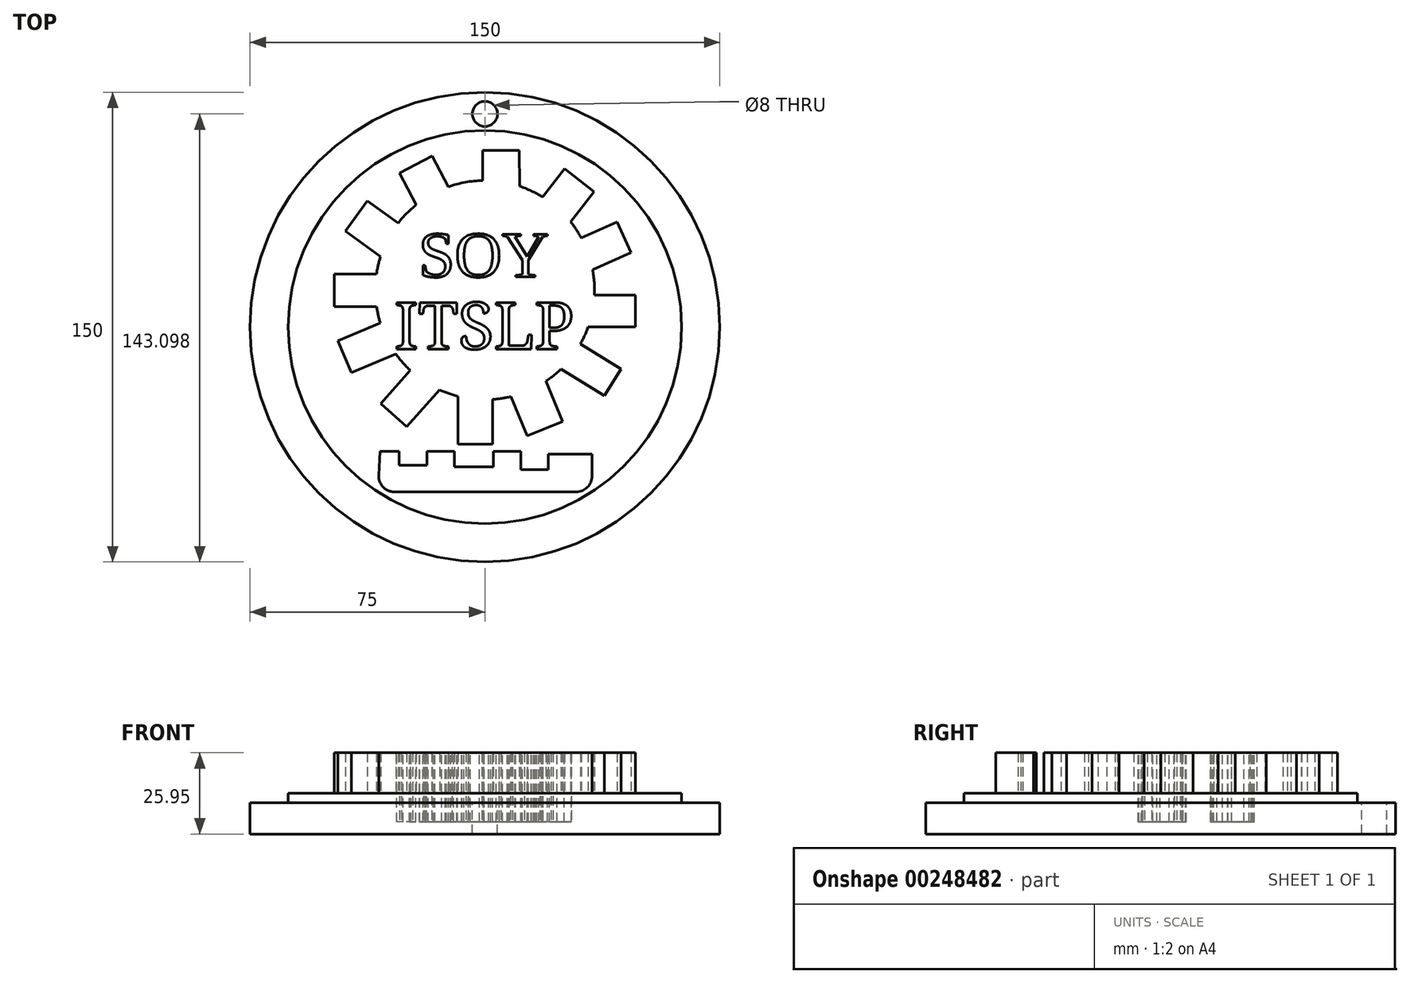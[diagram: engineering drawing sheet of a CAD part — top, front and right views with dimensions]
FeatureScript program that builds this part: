
annotation { "Feature Type Name" : "Feature", "Feature Type Description" : "" }
export const myFeature = defineFeature(function(context is Context, id is Id, definition is map)
    precondition{}
    {
        {
            var Q0;
            Q0=qCreatedBy(makeId("Top.planeOp"),FACE);
            var sketch = newSketch(context, id + "F0", { "sketchPlane" : qUnion([Q0])});
            skCircle(sketch, "E0", {"center": v(0, 0) * mm, "radius": 75 * mm});
            skSolve(sketch);
        }
        {
            var Q0;
            Q0=makeQuery(id+"F0.imprint","IMPRINT",FACE,{"disambiguationData":[TD([[makeQuery(id+"F0.imprint","IMPRINT",EDGE,{"derivedFrom":sQuery(id+"F0.wireOp",EDGE,"E0")}),1.0]])]});
            var sketch = newSketch(context, id + "F1", { "sketchPlane" : qUnion([Q0])});
            skCircle(sketch, "E1.0", {"center": v(0, 0) * mm, "radius": 62.8 * mm});
            skSolve(sketch);
        }
        {
            var Q0;
            Q0=makeQuery(id+"F0.imprint","IMPRINT",FACE,{"disambiguationData":[TD([[makeQuery(id+"F0.imprint","IMPRINT",EDGE,{"derivedFrom":sQuery(id+"F0.wireOp",EDGE,"E0")}),1.0]])]});
            extrude(context, id + "F2", {"entities" : qUnion([Q0]), "depth" : 10 * mm});
        }
        {
            var Q0;
            Q0 = qSketchRegion(id + "F1", true);
            extrude(context, id + "F3", {"entities" : qUnion([Q0]), "operationType" : NewBodyOperationType.ADD, "depth" : 13 * mm});
        }
        {
            var Q0;
            Q0=makeQuery(id+"F2.opExtrude","CAP_FACE",FACE,{"disambiguationData":[OSD([sQuery(id+"F0.wireOp",EDGE,"E0")])],"isStart":false});
            var sketch = newSketch(context, id + "F4", { "sketchPlane" : qUnion([Q0])});
            skLineSegment(sketch, "E2", {"start": v(-31.43, 68.1) * mm, "end": v(31.43, 68.1) * mm, "construction": true});
            skCircle(sketch, "E3", {"center": v(0, 68.1) * mm, "radius": 4 * mm});
            skSolve(sketch);
        }
        {
            var Q0;
            Q0=makeQuery(id+"F4.imprint","IMPRINT",FACE,{"disambiguationData":[TD([[makeQuery(id+"F4.imprint","IMPRINT",EDGE,{"derivedFrom":sQuery(id+"F4.wireOp",EDGE,"E3")}),1.0]])]});
            extrude(context, id + "F5", {"entities" : qUnion([Q0]), "operationType" : NewBodyOperationType.REMOVE, "oppositeDirection" : true, "depth" : 25.4 * mm});
        }
        {
            var Q0;
            Q0=makeQuery(id+"F3.opExtrude","CAP_FACE",FACE,{"disambiguationData":[OSD([sQuery(id+"F1.wireOp",EDGE,"E1.0")])],"isStart":false});
            var sketch = newSketch(context, id + "F6", { "sketchPlane" : qUnion([Q0])});
            skLineSegment(sketch, "E4", {"start": v(-61.69, 11.8) * mm, "end": v(61.69, 11.8) * mm, "construction": true});
            skArc(sketch, "E5", {"start": v(-0.68, 46.8) * mm, "mid": v(-6.24, 46.25) * mm, "end": v(-11.65, 44.81) * mm});
            skPoint(sketch, "E6.end.orphan", {"position": v(25.38, 50.6) * mm});
            skLineSegment(sketch, "E7", {"start": v(-0.68, 46.8) * mm, "end": v(-0.68, 56.4) * mm});
            skLineSegment(sketch, "E8", {"start": v(-0.68, 56.4) * mm, "end": v(10.94, 56.4) * mm});
            skLineSegment(sketch, "E9", {"start": v(10.94, 56.4) * mm, "end": v(11.06, 45.02) * mm});
            skLineSegment(sketch, "E10", {"start": v(18.4, 41.58) * mm, "end": v(25.38, 50.6) * mm});
            skLineSegment(sketch, "E11", {"start": v(25.38, 50.6) * mm, "end": v(34.85, 43.29) * mm});
            skLineSegment(sketch, "E12", {"start": v(34.85, 43.29) * mm, "end": v(27.38, 33.61) * mm});
            skLineSegment(sketch, "E13", {"start": v(30.77, 28.5) * mm, "end": v(42.2, 33.61) * mm});
            skLineSegment(sketch, "E14", {"start": v(42.2, 33.61) * mm, "end": v(46.6, 23.76) * mm});
            skLineSegment(sketch, "E15", {"start": v(46.6, 23.76) * mm, "end": v(34.4, 18.3) * mm});
            skArc(sketch, "E16.trimOffspring", {"start": v(18.4, 41.58) * mm, "mid": v(14.83, 43.51) * mm, "end": v(11.06, 45.02) * mm});
            skArc(sketch, "E17.trimOffspring", {"start": v(30.77, 28.5) * mm, "mid": v(29.18, 31.13) * mm, "end": v(27.38, 33.61) * mm});
            skLineSegment(sketch, "E18", {"start": v(34.97, 10.27) * mm, "end": v(48.04, 10.27) * mm});
            skLineSegment(sketch, "E19", {"start": v(48.04, 10.27) * mm, "end": v(48.04, 0) * mm});
            skLineSegment(sketch, "E20", {"start": v(48.04, 0) * mm, "end": v(32.95, 0) * mm});
            skLineSegment(sketch, "E21", {"start": v(30.5, -5.36) * mm, "end": v(43.43, -13.36) * mm});
            skLineSegment(sketch, "E22", {"start": v(43.43, -13.36) * mm, "end": v(38.14, -21.91) * mm});
            skLineSegment(sketch, "E23", {"start": v(38.14, -21.91) * mm, "end": v(24.32, -13.36) * mm});
            skLineSegment(sketch, "E24", {"start": v(19.5, -17.26) * mm, "end": v(24.8, -30.12) * mm});
            skLineSegment(sketch, "E25", {"start": v(24.8, -30.12) * mm, "end": v(13.44, -34.8) * mm});
            skLineSegment(sketch, "E26", {"start": v(13.44, -34.8) * mm, "end": v(8.24, -22.2) * mm});
            skLineSegment(sketch, "E27", {"start": v(2.4, -23.1) * mm, "end": v(2.4, -37.38) * mm});
            skLineSegment(sketch, "E28", {"start": v(2.4, -37.38) * mm, "end": v(-8.63, -37.38) * mm});
            skLineSegment(sketch, "E29", {"start": v(-8.63, -37.38) * mm, "end": v(-8.63, -22.1) * mm});
            skLineSegment(sketch, "E30", {"start": v(-14.45, -20.07) * mm, "end": v(-25, -31.83) * mm});
            skLineSegment(sketch, "E31", {"start": v(-25, -31.83) * mm, "end": v(-33.27, -24.4) * mm});
            skLineSegment(sketch, "E32", {"start": v(-33.27, -24.4) * mm, "end": v(-23.8, -13.85) * mm});
            skLineSegment(sketch, "E33", {"start": v(-28.44, -8.59) * mm, "end": v(-42.6, -14.56) * mm});
            skLineSegment(sketch, "E34", {"start": v(-42.6, -14.56) * mm, "end": v(-46.9, -4.36) * mm});
            skLineSegment(sketch, "E35", {"start": v(-46.9, -4.36) * mm, "end": v(-33.4, 1.34) * mm});
            skLineSegment(sketch, "E36", {"start": v(-34.6, 6.55) * mm, "end": v(-48.07, 6.55) * mm});
            skLineSegment(sketch, "E37", {"start": v(-48.07, 6.55) * mm, "end": v(-48.07, 16.96) * mm});
            skLineSegment(sketch, "E38", {"start": v(-48.07, 16.96) * mm, "end": v(-34.62, 16.96) * mm});
            skLineSegment(sketch, "E39", {"start": v(-33.32, 22.53) * mm, "end": v(-44.55, 30.62) * mm});
            skLineSegment(sketch, "E40", {"start": v(-44.55, 30.62) * mm, "end": v(-37.56, 40.33) * mm});
            skLineSegment(sketch, "E41", {"start": v(-37.56, 40.33) * mm, "end": v(-27.69, 33.22) * mm});
            skLineSegment(sketch, "E42", {"start": v(-21.96, 39.06) * mm, "end": v(-27.27, 49.15) * mm});
            skLineSegment(sketch, "E43", {"start": v(-27.27, 49.15) * mm, "end": v(-16.81, 54.65) * mm});
            skLineSegment(sketch, "E44", {"start": v(-16.81, 54.65) * mm, "end": v(-11.65, 44.81) * mm});
            skArc(sketch, "E45.trimOffspring", {"start": v(-21.96, 39.06) * mm, "mid": v(-25, 36.3) * mm, "end": v(-27.69, 33.22) * mm});
            skArc(sketch, "E46.trimOffspring", {"start": v(-33.32, 22.53) * mm, "mid": v(-34.08, 19.77) * mm, "end": v(-34.62, 16.96) * mm});
            skArc(sketch, "E47.trimOffspring", {"start": v(-34.6, 6.55) * mm, "mid": v(-34.1, 3.92) * mm, "end": v(-33.4, 1.34) * mm});
            skArc(sketch, "E48.trimOffspring", {"start": v(-28.44, -8.59) * mm, "mid": v(-26.26, -11.33) * mm, "end": v(-23.8, -13.85) * mm});
            skArc(sketch, "E49.trimOffspring", {"start": v(-14.45, -20.07) * mm, "mid": v(-11.59, -21.22) * mm, "end": v(-8.63, -22.1) * mm});
            skArc(sketch, "E50.trimOffspring", {"start": v(2.4, -23.1) * mm, "mid": v(5.34, -22.78) * mm, "end": v(8.24, -22.2) * mm});
            skArc(sketch, "E51.trimOffspring", {"start": v(19.5, -17.26) * mm, "mid": v(22, -15.41) * mm, "end": v(24.32, -13.36) * mm});
            skArc(sketch, "E52.trimOffspring", {"start": v(30.5, -5.36) * mm, "mid": v(31.84, -2.73) * mm, "end": v(32.95, 0) * mm});
            skArc(sketch, "E53.trimOffspring", {"start": v(34.97, 10.27) * mm, "mid": v(34.91, 14.3) * mm, "end": v(34.4, 18.3) * mm});
            skLineSegment(sketch, "E54", {"start": v(-28.83, -52.68) * mm, "end": v(29.12, -52.68) * mm});
            skLineSegment(sketch, "E55", {"start": v(34.2, -47.6) * mm, "end": v(34.2, -40.6) * mm});
            skLineSegment(sketch, "E56", {"start": v(34.2, -40.6) * mm, "end": v(20.29, -40.6) * mm});
            skLineSegment(sketch, "E57", {"start": v(20.29, -40.6) * mm, "end": v(20.29, -45.56) * mm});
            skLineSegment(sketch, "E58", {"start": v(20.29, -45.56) * mm, "end": v(11.52, -45.56) * mm});
            skLineSegment(sketch, "E59", {"start": v(11.52, -45.56) * mm, "end": v(11.52, -39.71) * mm});
            skLineSegment(sketch, "E60", {"start": v(11.52, -39.71) * mm, "end": v(2.76, -39.71) * mm});
            skLineSegment(sketch, "E61", {"start": v(2.76, -39.71) * mm, "end": v(2.76, -44.68) * mm});
            skLineSegment(sketch, "E62", {"start": v(2.76, -44.68) * mm, "end": v(-9.8, -44.68) * mm});
            skLineSegment(sketch, "E63", {"start": v(-9.8, -44.68) * mm, "end": v(-9.8, -39.71) * mm});
            skLineSegment(sketch, "E64", {"start": v(-9.8, -39.71) * mm, "end": v(-18.57, -39.71) * mm});
            skLineSegment(sketch, "E65", {"start": v(-18.57, -39.71) * mm, "end": v(-18.57, -44.1) * mm});
            skLineSegment(sketch, "E66", {"start": v(-18.57, -44.1) * mm, "end": v(-27.33, -44.1) * mm});
            skLineSegment(sketch, "E67", {"start": v(-27.33, -44.1) * mm, "end": v(-27.33, -39.71) * mm});
            skLineSegment(sketch, "E68", {"start": v(-27.33, -39.71) * mm, "end": v(-33.47, -39.71) * mm});
            skLineSegment(sketch, "E69", {"start": v(-33.47, -39.71) * mm, "end": v(-33.9, -47.31) * mm});
            skPoint(sketch, "E70.visualSharp", {"position": v(-34.2, -52.68) * mm});
            skArc(sketch, "E70.filletArc", {"start": v(-33.9, -47.31) * mm, "mid": v(-32.52, -51.09) * mm, "end": v(-28.83, -52.68) * mm});
            skPoint(sketch, "E71.visualSharp", {"position": v(34.2, -52.68) * mm});
            skArc(sketch, "E71.filletArc", {"start": v(29.12, -52.68) * mm, "mid": v(32.71, -51.2) * mm, "end": v(34.2, -47.6) * mm});
            skSolve(sketch);
        }
        {
            var Q0;
            Q0 = qSketchRegion(id + "F6", true);
            extrude(context, id + "F7", {"entities" : qUnion([Q0]), "operationType" : NewBodyOperationType.ADD, "depth" : 12.95 * mm});
        }
        {
            var Q0;
            Q0=makeQuery(id+"F7.opExtrude","CAP_FACE",FACE,{"disambiguationData":[OSD([sQuery(id+"F6.wireOp",EDGE,"E5"),sQuery(id+"F6.wireOp",EDGE,"E7"),sQuery(id+"F6.wireOp",EDGE,"E8"),sQuery(id+"F6.wireOp",EDGE,"E9"),sQuery(id+"F6.wireOp",EDGE,"E10"),sQuery(id+"F6.wireOp",EDGE,"E11"),sQuery(id+"F6.wireOp",EDGE,"E12"),sQuery(id+"F6.wireOp",EDGE,"E13"),sQuery(id+"F6.wireOp",EDGE,"E14"),sQuery(id+"F6.wireOp",EDGE,"E15"),sQuery(id+"F6.wireOp",EDGE,"E16.trimOffspring"),sQuery(id+"F6.wireOp",EDGE,"E17.trimOffspring"),sQuery(id+"F6.wireOp",EDGE,"E18"),sQuery(id+"F6.wireOp",EDGE,"E19"),sQuery(id+"F6.wireOp",EDGE,"E20"),sQuery(id+"F6.wireOp",EDGE,"E21"),sQuery(id+"F6.wireOp",EDGE,"E22"),sQuery(id+"F6.wireOp",EDGE,"E23"),sQuery(id+"F6.wireOp",EDGE,"E24"),sQuery(id+"F6.wireOp",EDGE,"E25"),sQuery(id+"F6.wireOp",EDGE,"E26"),sQuery(id+"F6.wireOp",EDGE,"E27"),sQuery(id+"F6.wireOp",EDGE,"E28"),sQuery(id+"F6.wireOp",EDGE,"E29"),sQuery(id+"F6.wireOp",EDGE,"E30"),sQuery(id+"F6.wireOp",EDGE,"E31"),sQuery(id+"F6.wireOp",EDGE,"E32"),sQuery(id+"F6.wireOp",EDGE,"E33"),sQuery(id+"F6.wireOp",EDGE,"E34"),sQuery(id+"F6.wireOp",EDGE,"E35"),sQuery(id+"F6.wireOp",EDGE,"E36"),sQuery(id+"F6.wireOp",EDGE,"E37"),sQuery(id+"F6.wireOp",EDGE,"E38"),sQuery(id+"F6.wireOp",EDGE,"E39"),sQuery(id+"F6.wireOp",EDGE,"E40"),sQuery(id+"F6.wireOp",EDGE,"E41"),sQuery(id+"F6.wireOp",EDGE,"E42"),sQuery(id+"F6.wireOp",EDGE,"E43"),sQuery(id+"F6.wireOp",EDGE,"E44"),sQuery(id+"F6.wireOp",EDGE,"E45.trimOffspring"),sQuery(id+"F6.wireOp",EDGE,"E46.trimOffspring"),sQuery(id+"F6.wireOp",EDGE,"E47.trimOffspring"),sQuery(id+"F6.wireOp",EDGE,"E48.trimOffspring"),sQuery(id+"F6.wireOp",EDGE,"E49.trimOffspring"),sQuery(id+"F6.wireOp",EDGE,"E50.trimOffspring"),sQuery(id+"F6.wireOp",EDGE,"E51.trimOffspring"),sQuery(id+"F6.wireOp",EDGE,"E52.trimOffspring"),sQuery(id+"F6.wireOp",EDGE,"E53.trimOffspring")])],"isStart":false});
            var sketch = newSketch(context, id + "F8", { "sketchPlane" : qUnion([Q0])});
            skText(sketch, "E72", { "text": "SOY", "fontName": "Tinos-Regular.ttf"});
            skLineSegment(sketch, "E73", {"start": v(-27.69, 33.22) * mm, "end": v(27.38, 33.61) * mm, "construction": true});
            const initialGuessF8  = {"E72": [-0.02122, 0.01605, 1, 0, 0.015]};
            skSetInitialGuess(sketch, initialGuessF8);
            skSolve(sketch);
        }
        {
            var Q0;
            Q0 = qSketchRegion(id + "F8", true);
            extrude(context, id + "F9", {"entities" : qUnion([Q0]), "operationType" : NewBodyOperationType.REMOVE, "oppositeDirection" : true, "depth" : 22.1 * mm});
        }
        {
            var Q0;
            {var subQ0=sQuery(id+"F6.wireOp",EDGE,"E24");var subQ1=sQuery(id+"F6.wireOp",EDGE,"E45.trimOffspring");var subQ2=sQuery(id+"F6.wireOp",EDGE,"E43");var subQ3=sQuery(id+"F6.wireOp",EDGE,"E27");var subQ4=sQuery(id+"F6.wireOp",EDGE,"E25");var subQ5=sQuery(id+"F6.wireOp",EDGE,"E46.trimOffspring");var subQ6=sQuery(id+"F6.wireOp",EDGE,"E19");var subQ7=sQuery(id+"F6.wireOp",EDGE,"E32");var subQ8=sQuery(id+"F6.wireOp",EDGE,"E9");var subQ9=sQuery(id+"F6.wireOp",EDGE,"E13");var subQ10=sQuery(id+"F6.wireOp",EDGE,"E18");var subQ11=sQuery(id+"F6.wireOp",EDGE,"E31");var subQ12=sQuery(id+"F6.wireOp",EDGE,"E12");var subQ13=sQuery(id+"F6.wireOp",EDGE,"E22");var subQ14=sQuery(id+"F6.wireOp",EDGE,"E7");var subQ15=sQuery(id+"F6.wireOp",EDGE,"E20");var subQ16=sQuery(id+"F6.wireOp",EDGE,"E14");var subQ17=sQuery(id+"F6.wireOp",EDGE,"E26");var subQ18=sQuery(id+"F6.wireOp",EDGE,"E47.trimOffspring");var subQ19=sQuery(id+"F6.wireOp",EDGE,"E33");var subQ20=sQuery(id+"F6.wireOp",EDGE,"E5");var subQ21=sQuery(id+"F6.wireOp",EDGE,"E23");var subQ22=sQuery(id+"F6.wireOp",EDGE,"E44");var subQ23=sQuery(id+"F6.wireOp",EDGE,"E10");var subQ24=sQuery(id+"F6.wireOp",EDGE,"E34");var subQ25=sQuery(id+"F6.wireOp",EDGE,"E8");var subQ26=sQuery(id+"F6.wireOp",EDGE,"E21");var subQ27=sQuery(id+"F6.wireOp",EDGE,"E28");var subQ28=sQuery(id+"F6.wireOp",EDGE,"E15");var subQ29=sQuery(id+"F6.wireOp",EDGE,"E41");var subQ30=sQuery(id+"F6.wireOp",EDGE,"E11");var subQ31=sQuery(id+"F6.wireOp",EDGE,"E16.trimOffspring");var subQ32=sQuery(id+"F6.wireOp",EDGE,"E29");var subQ33=sQuery(id+"F6.wireOp",EDGE,"E17.trimOffspring");var subQ34=sQuery(id+"F6.wireOp",EDGE,"E30");var subQ35=sQuery(id+"F6.wireOp",EDGE,"E35");var subQ36=sQuery(id+"F6.wireOp",EDGE,"E36");var subQ37=sQuery(id+"F6.wireOp",EDGE,"E37");var subQ38=sQuery(id+"F6.wireOp",EDGE,"E38");var subQ39=sQuery(id+"F6.wireOp",EDGE,"E42");var subQ40=sQuery(id+"F6.wireOp",EDGE,"E52.trimOffspring");var subQ41=sQuery(id+"F6.wireOp",EDGE,"E39");var subQ42=sQuery(id+"F6.wireOp",EDGE,"E53.trimOffspring");var subQ43=sQuery(id+"F6.wireOp",EDGE,"E40");var subQ44=sQuery(id+"F6.wireOp",EDGE,"E50.trimOffspring");var subQ45=sQuery(id+"F6.wireOp",EDGE,"E51.trimOffspring");var subQ46=sQuery(id+"F6.wireOp",EDGE,"E48.trimOffspring");var subQ47=sQuery(id+"F6.wireOp",EDGE,"E49.trimOffspring");Q0=makeQuery(id+"F9.boolean.opBoolean","SPLIT",FACE,{"disambiguationData":[TD([makeQuery(id+"F7.opExtrude","SWEPT_FACE",FACE,{"disambiguationData":[OSD([subQ20])]})])],"derivedFrom":makeQuery(id+"F7.opExtrude","CAP_FACE",FACE,{"disambiguationData":[OSD([subQ20,subQ14,subQ25,subQ8,subQ23,subQ30,subQ12,subQ9,subQ16,subQ28,subQ31,subQ33,subQ10,subQ6,subQ15,subQ26,subQ13,subQ21,subQ0,subQ4,subQ17,subQ3,subQ27,subQ32,subQ34,subQ11,subQ7,subQ19,subQ24,subQ35,subQ36,subQ37,subQ38,subQ41,subQ43,subQ29,subQ39,subQ2,subQ22,subQ1,subQ5,subQ18,subQ46,subQ47,subQ44,subQ45,subQ40,subQ42])],"isStart":false})});}
            var sketch = newSketch(context, id + "F10", { "sketchPlane" : qUnion([Q0])});
            skText(sketch, "E74", { "text": "ITSLP", "fontName": "NotoSerif-Regular.ttf"});
            const initialGuessF10  = {"E74": [-0.02893, -0.00701, 1, 0, 0.015]};
            skSetInitialGuess(sketch, initialGuessF10);
            skSolve(sketch);
        }
        {
            var Q0;
            Q0 = qSketchRegion(id + "F10", true);
            extrude(context, id + "F11", {"entities" : qUnion([Q0]), "operationType" : NewBodyOperationType.REMOVE, "oppositeDirection" : true, "depth" : 22.1 * mm});
        }
    });
